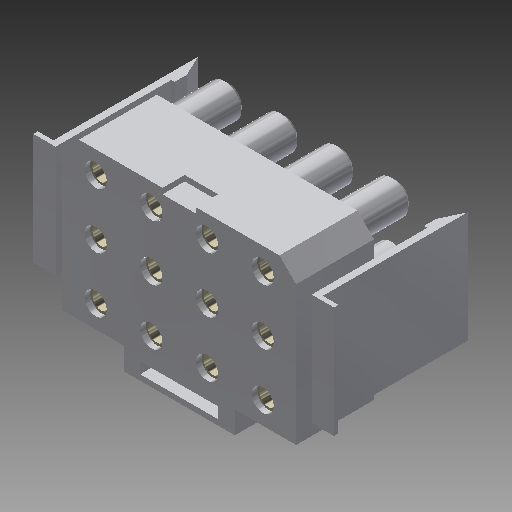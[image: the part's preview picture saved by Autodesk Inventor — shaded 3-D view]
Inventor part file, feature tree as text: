
AUTODESK INVENTOR PART (.ipt)
format: ipt  version: 2019 (Build 230136000, 136)  size: 480,768 bytes
history: native  units: in
note: dims shown in document units (in); Inventor stores cm internally (conversion verified against a paired STEP export)
features: extrude x6, sketch x4, pattern_linear x2, chamfer x2, mirror x1, plane x1, revolve x1, other x1
ambient origin geometry x8: Origin, YZ Plane, XZ Plane, XY Plane, X Axis, Y Axis, Z Axis, Center Point
bodies: Solid1 (feature_tree), Solid2 (feature_tree)
feature tree (18):
  sketch  "Sketch1"  dims[d7=0.0in d9=0.0in]
  extrude  "Extrusion1"  TaperAngle=0.0deg  [1 undecoded]
  extrude  "Extrusion2"  Depth=0.05in
  extrude  "Extrusion3"  Depth=0.125in TaperAngle=45.0deg
  pattern_linear  "Rectangular Pattern1"  Spacing1=0.025in  [1 undecoded]
  chamfer  "Chamfer1"  Distance=0.1in
  extrude  "Extrusion4"  Depth=0.05in
  sketch  "Sketch3"  dims[d20=0.025in d24=0.125in d25=45.0deg]
  extrude  "Extrusion5"  Depth=0.1in
  extrude  "Extrusion6"  Depth=0.02in
  mirror  "Mirror1"
  chamfer  "Chamfer2"  Distance=0.02in
  plane  "Work Plane1"
  revolve  "Revolution1"  [1 undecoded]
  pattern_linear  "Rectangular Pattern2"  Spacing1=0.03in  [1 undecoded]
  sketch  "Sketch2"  dims[d10=0.25in d11=0.0in d18=0.05in]
  other  "Work Axis1"
  sketch  "Sketch4"  dims[d26=0.15in d27=0.025in d28=0.1in d29=0.0in d30=0.05in d31=0.1in d32=0.02in d34=0.02in d35=0.1in d36=0.03in d37=0.015in d38=0.1718in d39=0.65in d40=0.15in d41=0.075in d42=0.0in d43=0.5in d44=0.0in d45=0.02in d46=0.125in d47=45.0deg d48=90.0deg d49=0.05in d51=0.9963in d53=0.24in d54=0.025in d55=0.225in d56=0.01in d57=0.01in d58=0.01in d59=90.0deg d60=1.5748in d62=0.25in d63=1.1811in d65=0.25in]
note: 4 required parameter values undecoded (feature->parameter linkage not recoverable at this tier; creation-order binding heuristic only, values carry confidence <= 0.55)